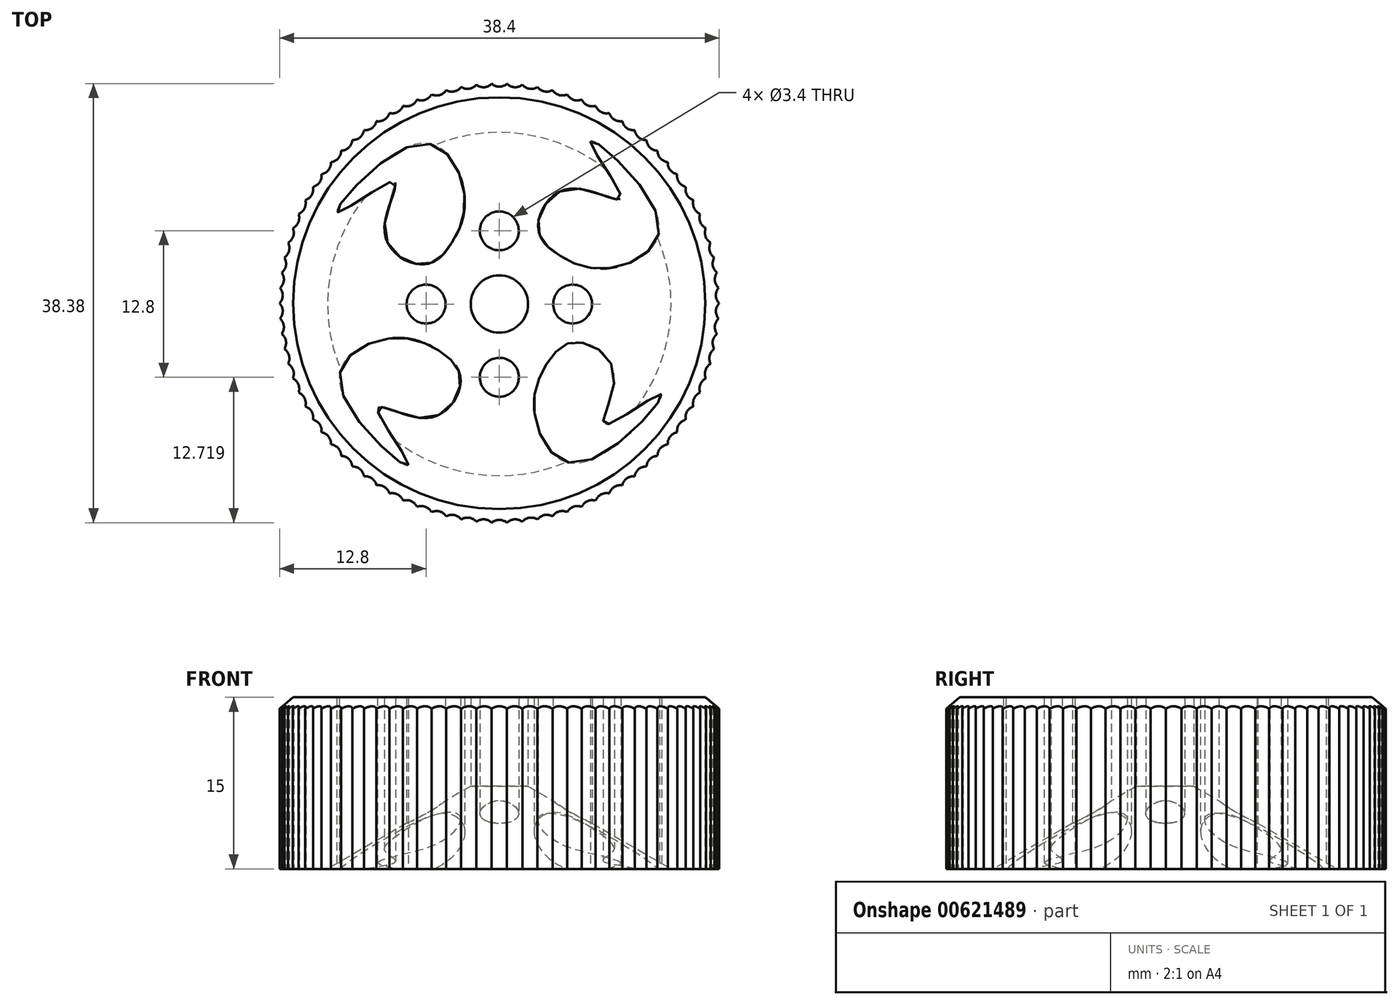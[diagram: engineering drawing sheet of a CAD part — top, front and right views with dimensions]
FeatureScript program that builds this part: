
annotation { "Feature Type Name" : "Feature", "Feature Type Description" : "" }
export const myFeature = defineFeature(function(context is Context, id is Id, definition is map)
    precondition{}
    {
        {
            var Q0;
            Q0=qCreatedBy(makeId("Top.planeOp"),FACE);
            var sketch = newSketch(context, id + "F0", { "sketchPlane" : qUnion([Q0])});
            skCircle(sketch, "E0", {"center": v(0, -0.07) * mm, "radius": 20 * mm});
            skCircle(sketch, "E1", {"center": v(0, -0.07) * mm, "radius": 15 * mm});
            skCircle(sketch, "E2", {"center": v(0, -0.07) * mm, "radius": 2.5 * mm});
            skCircle(sketch, "E3", {"center": v(0, 6.33) * mm, "radius": 1.7 * mm});
            skCircle(sketch, "E4", {"center": v(6.4, -0.07) * mm, "radius": 1.7 * mm});
            skCircle(sketch, "E5", {"center": v(0, -6.47) * mm, "radius": 1.7 * mm});
            skCircle(sketch, "E6", {"center": v(-6.4, -0.07) * mm, "radius": 1.7 * mm});
            skSolve(sketch);
        }
        {
            var Q0;
            Q0=makeQuery(id+"F0.imprint","IMPRINT",FACE,{"disambiguationData":[TD([[makeQuery(id+"F0.imprint","IMPRINT",EDGE,{"derivedFrom":sQuery(id+"F0.wireOp",EDGE,"E0")}),1.0]])]});
            var Q1;
            Q1=makeQuery(id+"F0.imprint","IMPRINT",FACE,{"disambiguationData":[TD([[makeQuery(id+"F0.imprint","IMPRINT",EDGE,{"derivedFrom":sQuery(id+"F0.wireOp",EDGE,"E1")}),1.0]])]});
            extrude(context, id + "F1", {"entities" : qUnion([Q0, Q1]), "depth" : 15 * mm, "offsetDistance" : 25 * mm});
        }
        {
            var Q0;
            Q0=makeQuery(id+"F0.imprint","IMPRINT",FACE,{"disambiguationData":[TD([[makeQuery(id+"F0.imprint","IMPRINT",EDGE,{"derivedFrom":sQuery(id+"F0.wireOp",EDGE,"E1")}),1.0]])]});
            var Q1;
            Q1=makeQuery(id+"F0.imprint","IMPRINT",FACE,{"disambiguationData":[TD([[makeQuery(id+"F0.imprint","IMPRINT",EDGE,{"derivedFrom":sQuery(id+"F0.wireOp",EDGE,"E5")}),1.0]])]});
            var Q2;
            Q2=makeQuery(id+"F0.imprint","IMPRINT",FACE,{"disambiguationData":[TD([[makeQuery(id+"F0.imprint","IMPRINT",EDGE,{"derivedFrom":sQuery(id+"F0.wireOp",EDGE,"E4")}),1.0]])]});
            var Q3;
            Q3=makeQuery(id+"F0.imprint","IMPRINT",FACE,{"disambiguationData":[TD([[makeQuery(id+"F0.imprint","IMPRINT",EDGE,{"derivedFrom":sQuery(id+"F0.wireOp",EDGE,"E2")}),1.0]])]});
            var Q4;
            Q4=makeQuery(id+"F0.imprint","IMPRINT",FACE,{"disambiguationData":[TD([[makeQuery(id+"F0.imprint","IMPRINT",EDGE,{"derivedFrom":sQuery(id+"F0.wireOp",EDGE,"E3")}),1.0]])]});
            var Q5;
            Q5=makeQuery(id+"F0.imprint","IMPRINT",FACE,{"disambiguationData":[TD([[makeQuery(id+"F0.imprint","IMPRINT",EDGE,{"derivedFrom":sQuery(id+"F0.wireOp",EDGE,"E6")}),1.0]])]});
            extrude(context, id + "F2", {"entities" : qUnion([Q0, Q1, Q2, Q3, Q4, Q5]), "operationType" : NewBodyOperationType.REMOVE, "depth" : 8 * mm, "offsetDistance" : 25 * mm, "hasDraft" : true, "draftAngle" : 60 * degree, "draftPullDirection" : true});
        }
        {
            var Q0;
            Q0=qCreatedBy(makeId("Top.planeOp"),FACE);
            var sketch = newSketch(context, id + "F3", { "sketchPlane" : qUnion([Q0])});
            skCircle(sketch, "E7", {"center": v(0, 19.93) * mm, "radius": 1 * mm});
            skSolve(sketch);
        }
        {
            var Q0;
            Q0=makeQuery(id+"F3.imprint","IMPRINT",FACE,{"disambiguationData":[TD([[makeQuery(id+"F3.imprint","IMPRINT",EDGE,{"derivedFrom":sQuery(id+"F3.wireOp",EDGE,"E7")}),1.0]])]});
            extrude(context, id + "F4", {"entities" : qUnion([Q0]), "depth" : 25 * mm, "offsetDistance" : 25 * mm});
        }
        {
            var Q0;
            Q0=qCreatedBy(makeId("Right.planeOp"),FACE);
            var sketch = newSketch(context, id + "F5", { "sketchPlane" : qUnion([Q0])});
            skLineSegment(sketch, "E8", {"start": v(0, 25.16) * mm, "end": v(0, -9.7) * mm});
            skSolve(sketch);
        }
        {
            var Q0;
            Q0=makeQuery(id+"F4.opExtrude","SWEPT_BODY",BODY,{"disambiguationData":[OSD([sQuery(id+"F3.wireOp",EDGE,"E7")])]});
            var Q1;
            Q1=sQuery(id+"F5.wireOp",EDGE,"E8");
            circularPattern(context, id + "F6", {"operationType" : NewBodyOperationType.REMOVE, "entities" : qUnion([Q0]), "axis" : qUnion([Q1]), "angle" : 360 * degree, "instanceCount" : 90, "equalSpace" : true});
        }
        {
            var Q0;
            Q0=makeQuery(id+"F1.opExtrude","CAP_FACE",FACE,{"disambiguationData":[OSD([sQuery(id+"F0.wireOp",EDGE,"E0"),sQuery(id+"F0.wireOp",EDGE,"E2"),sQuery(id+"F0.wireOp",EDGE,"E3"),sQuery(id+"F0.wireOp",EDGE,"E4"),sQuery(id+"F0.wireOp",EDGE,"E5"),sQuery(id+"F0.wireOp",EDGE,"E6")])],"isStart":false});
            var sketch = newSketch(context, id + "F7", { "sketchPlane" : qUnion([Q0])});
            skCircle(sketch, "E9", {"center": v(0, 0) * mm, "radius": 18 * mm});
            skCircle(sketch, "E10", {"center": v(0, 0) * mm, "radius": 20.5 * mm});
            skSolve(sketch);
        }
        {
            var Q0;
            Q0=makeQuery(id+"F7.imprint","IMPRINT",FACE,{"disambiguationData":[TD([[makeQuery(id+"F7.imprint","IMPRINT",EDGE,{"derivedFrom":sQuery(id+"F7.wireOp",EDGE,"E9")}),-1.0]])]});
            var Q1;
            Q1=makeQuery(id+"F7.imprint","IMPRINT",FACE,{"disambiguationData":[TD([[makeQuery(id+"F7.imprint","IMPRINT",EDGE,{"derivedFrom":sQuery(id+"F7.wireOp",EDGE,"E10")}),1.0]])]});
            extrude(context, id + "F8", {"entities" : qUnion([Q0, Q1]), "operationType" : NewBodyOperationType.REMOVE, "oppositeDirection" : true, "depth" : 1.5 * mm, "offsetDistance" : 25 * mm, "hasDraft" : true, "draftAngle" : 50 * degree, "draftPullDirection" : true});
        }
        {
            var Q0;
            Q0=makeQuery(id+"F0.imprint","IMPRINT",FACE,{"disambiguationData":[TD([[makeQuery(id+"F0.imprint","IMPRINT",EDGE,{"derivedFrom":sQuery(id+"F0.wireOp",EDGE,"E0")}),1.0]])]});
            var sketch = newSketch(context, id + "F9", { "sketchPlane" : qUnion([Q0])});
            skFitSpline(sketch, "E11", {"points": [v(-5.31, -4.13) * mm, v(-9.74, -3.09) * mm, v(-13.94, -7.12) * mm, v(-7.96, -14.14) * mm, v(-10.63, -9.24) * mm, v(-6.3, -10.03) * mm, v(-3.38, -6.7) * mm, v(-5.31, -4.13) * mm]});
            skSolve(sketch);
        }
        {
            var Q0;
            Q0 = qSketchRegion(id + "F9", true);
            extrude(context, id + "F10", {"entities" : qUnion([Q0]), "depth" : 25 * mm, "offsetDistance" : 25 * mm});
        }
        {
            var Q0;
            Q0=makeQuery(id+"F10.opExtrude","SWEPT_BODY",BODY,{"disambiguationData":[OSD([sQuery(id+"F9.wireOp",EDGE,"E11")])]});
            var Q1;
            Q1=sQuery(id+"F5.wireOp",EDGE,"E8");
            var Q2;
            Q2=makeQuery(id+"F1.opExtrude","SWEPT_BODY",BODY,{"disambiguationData":[OSD([sQuery(id+"F0.wireOp",EDGE,"E0"),sQuery(id+"F0.wireOp",EDGE,"E2"),sQuery(id+"F0.wireOp",EDGE,"E3"),sQuery(id+"F0.wireOp",EDGE,"E4"),sQuery(id+"F0.wireOp",EDGE,"E5"),sQuery(id+"F0.wireOp",EDGE,"E6")])]});
            circularPattern(context, id + "F11", {"operationType" : NewBodyOperationType.REMOVE, "entities" : qUnion([Q0]), "axis" : qUnion([Q1]), "angle" : 360 * degree, "instanceCount" : 4, "equalSpace" : true});
        }
    });
